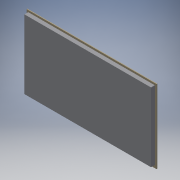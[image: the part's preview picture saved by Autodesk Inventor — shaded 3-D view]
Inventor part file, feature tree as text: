
AUTODESK INVENTOR PART (.ipt)
format: ipt  version: 2019 (Build 230136000, 136)  size: 99,840 bytes
history: native  units: mm
features: other x6, reference x4, extrude x2, sketch x2
ambient origin geometry x8: Origin, YZ Plane, XZ Plane, XY Plane, X Axis, Y Axis, Z Axis, Center Point
bodies: Solid1 (feature_tree)
feature tree (14):
  extrude  "Extrusion1"  Depth=861.06mm
  extrude  "Extrusion2"  Depth=25.4mm TaperAngle=0.0deg
  sketch  "Sketch1"  dims[d0=4.7625mm d1=0.0mm d2=861.06mm]
  sketch  "Sketch2"  dims[d3=487.68mm d4=25.4mm d5=0.0mm]
  reference  "Reference1"
  reference  "Reference2"
  reference  "Reference3"
  reference  "Reference4"
  parser-record x1  (decoder bookkeeping rows leaked as tree rows — omitted from the tree; the rows remain in map.json)
  other  "enclosure.iam"
  other  "1515-S-BLACK_rear_vert_post:2"
  other  "1515-S-BLACK_rear_top_cross:1"
  other  "1515-S-BLACK_rear_vert_post:1"
  other  "1530-S-BLACK_base_front:2"
note: 1 file-system path scrubbed to <path> (originals preserved in map.json)
